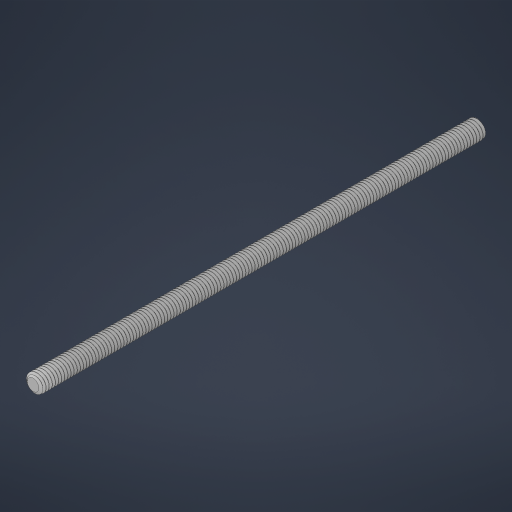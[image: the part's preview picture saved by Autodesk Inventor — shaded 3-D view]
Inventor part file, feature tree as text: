
AUTODESK INVENTOR PART (.ipt)
format: ipt  version: 2023 (Build 270158000, 158)  size: 3,337,728 bytes
history: native  units: in
note: dims shown in document units (in); Inventor stores cm internally (conversion verified against a paired STEP export)
features: mirror x1
ambient origin geometry x8: Origin, YZ Plane, XZ Plane, XY Plane, X Axis, Y Axis, Z Axis, Center Point
bodies: Solid1 (feature_tree)
feature tree (1):
  mirror  "Mirror1"
